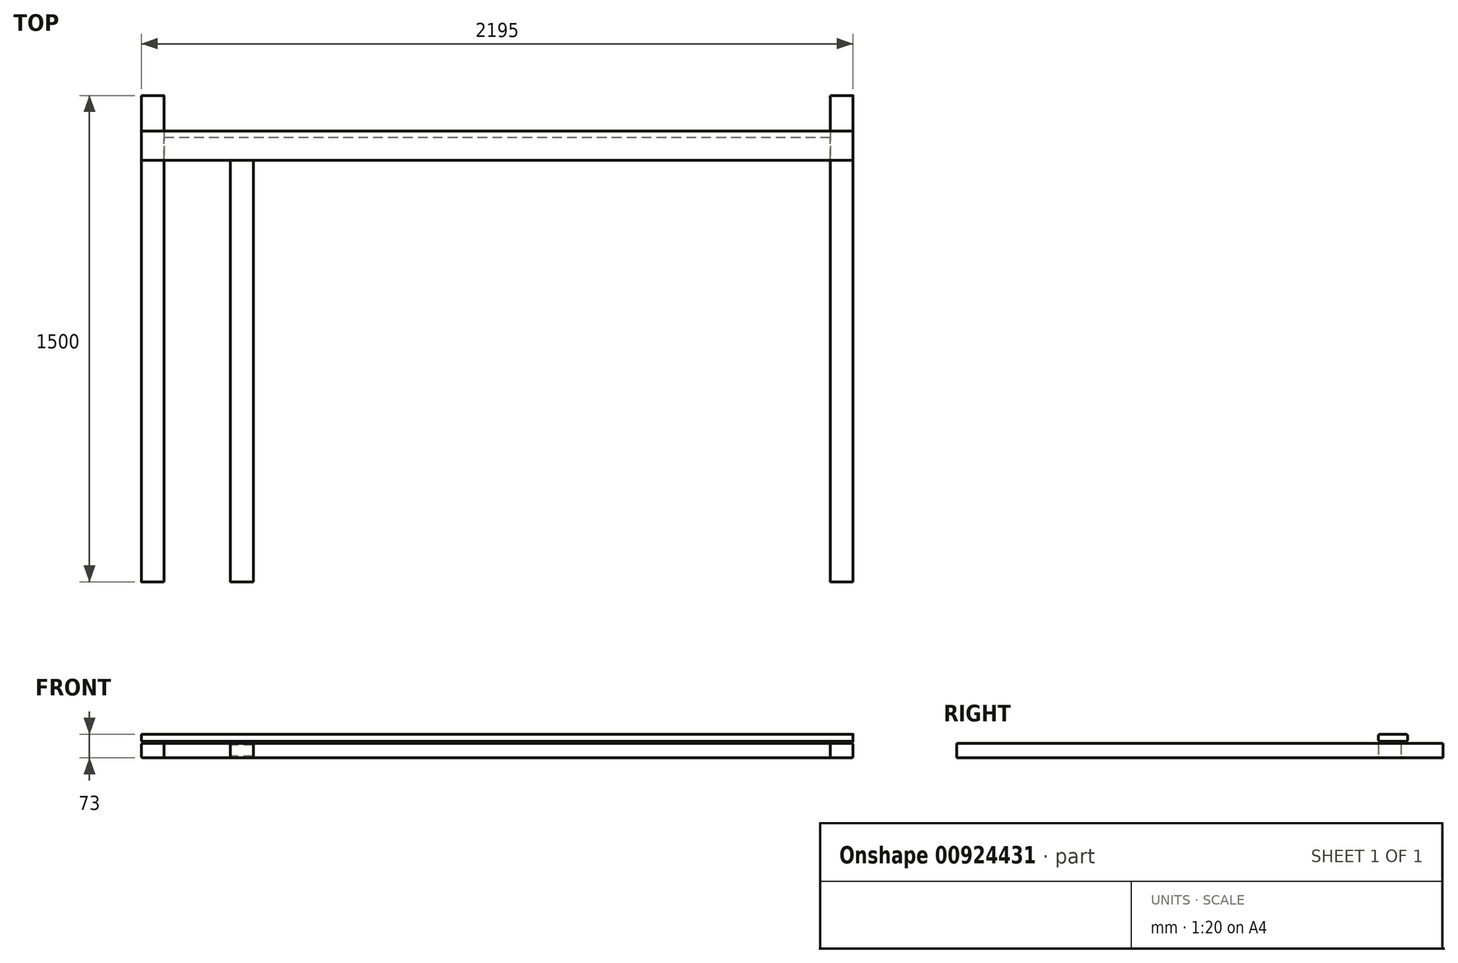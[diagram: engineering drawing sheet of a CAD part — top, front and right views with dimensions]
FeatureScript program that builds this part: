
annotation { "Feature Type Name" : "Feature", "Feature Type Description" : "" }
export const myFeature = defineFeature(function(context is Context, id is Id, definition is map)
    precondition{}
    {
        {
            var Q0;
            Q0=qCreatedBy(makeId("Front.planeOp"),FACE);
            var sketch = newSketch(context, id + "F0", { "sketchPlane" : qUnion([Q0])});
            skLineSegment(sketch, "E0.bottom", {"start": v(-5, 0) * mm, "end": v(-65, 0) * mm});
            skLineSegment(sketch, "E0.top", {"start": v(-5, 45) * mm, "end": v(-65, 45) * mm});
            skLineSegment(sketch, "E0.left", {"start": v(0, 5) * mm, "end": v(0, 40) * mm});
            skLineSegment(sketch, "E0.right", {"start": v(-70, 5) * mm, "end": v(-70, 40) * mm});
            skPoint(sketch, "E1.visualSharp", {"position": v(-70, 45) * mm});
            skArc(sketch, "E1.filletArc", {"start": v(-65, 45) * mm, "mid": v(-68.54, 43.54) * mm, "end": v(-70, 40) * mm});
            skPoint(sketch, "E2.visualSharp", {"position": v(0, 45) * mm});
            skArc(sketch, "E2.filletArc", {"start": v(0, 40) * mm, "mid": v(-1.46, 43.54) * mm, "end": v(-5, 45) * mm});
            skPoint(sketch, "E3.visualSharp", {"position": v(0, 0) * mm});
            skArc(sketch, "E3.filletArc", {"start": v(-5, 0) * mm, "mid": v(-1.46, 1.46) * mm, "end": v(0, 5) * mm});
            skPoint(sketch, "E4.visualSharp", {"position": v(-70, 0) * mm});
            skArc(sketch, "E4.filletArc", {"start": v(-70, 5) * mm, "mid": v(-68.54, 1.46) * mm, "end": v(-65, 0) * mm});
            skLineSegment(sketch, "E5.bottom", {"start": v(2060, 0) * mm, "end": v(2120, 0) * mm});
            skLineSegment(sketch, "E5.top", {"start": v(2060, 45) * mm, "end": v(2120, 45) * mm});
            skLineSegment(sketch, "E5.left", {"start": v(2055, 5) * mm, "end": v(2055, 40) * mm});
            skLineSegment(sketch, "E5.right", {"start": v(2125, 5) * mm, "end": v(2125, 40) * mm});
            skPoint(sketch, "E6.visualSharp", {"position": v(2055, 45) * mm});
            skArc(sketch, "E6.filletArc", {"start": v(2060, 45) * mm, "mid": v(2056.46, 43.54) * mm, "end": v(2055, 40) * mm});
            skPoint(sketch, "E7.visualSharp", {"position": v(2125, 45) * mm});
            skArc(sketch, "E7.filletArc", {"start": v(2125, 40) * mm, "mid": v(2123.54, 43.54) * mm, "end": v(2120, 45) * mm});
            skPoint(sketch, "E8.visualSharp", {"position": v(2125, 0) * mm});
            skArc(sketch, "E8.filletArc", {"start": v(2120, 0) * mm, "mid": v(2123.54, 1.46) * mm, "end": v(2125, 5) * mm});
            skPoint(sketch, "E9.visualSharp", {"position": v(2055, 0) * mm});
            skArc(sketch, "E9.filletArc", {"start": v(2055, 5) * mm, "mid": v(2056.46, 1.46) * mm, "end": v(2060, 0) * mm});
            skSolve(sketch);
        }
        {
            var Q0;
            Q0 = qSketchRegion(id + "F0", true);
            extrude(context, id + "F1", {"entities" : qUnion([Q0]), "oppositeDirection" : true, "depth" : 1500 * mm, "offsetDistance" : 25 * mm});
        }
        {
            var Q0;
            Q0=makeQuery(id+"F1.opExtrude","SWEPT_FACE",FACE,{"disambiguationData":[OSD([sQuery(id+"F0.wireOp",EDGE,"E0.left")])]});
            var sketch = newSketch(context, id + "F2", { "sketchPlane" : qUnion([Q0])});
            skLineSegment(sketch, "E10.bottom", {"start": v(1305, 45) * mm, "end": v(1365, 45) * mm});
            skLineSegment(sketch, "E10.top", {"start": v(1305, 0) * mm, "end": v(1365, 0) * mm});
            skLineSegment(sketch, "E10.left", {"start": v(1300, 40) * mm, "end": v(1300, 5) * mm});
            skLineSegment(sketch, "E10.right", {"start": v(1370, 40) * mm, "end": v(1370, 5) * mm});
            skPoint(sketch, "E11.visualSharp", {"position": v(1300, 45) * mm});
            skArc(sketch, "E11.filletArc", {"start": v(1305, 45) * mm, "mid": v(1301.46, 43.54) * mm, "end": v(1300, 40) * mm});
            skPoint(sketch, "E12.visualSharp", {"position": v(1370, 45) * mm});
            skArc(sketch, "E12.filletArc", {"start": v(1370, 40) * mm, "mid": v(1368.54, 43.54) * mm, "end": v(1365, 45) * mm});
            skPoint(sketch, "E13.visualSharp", {"position": v(1370, 0) * mm});
            skArc(sketch, "E13.filletArc", {"start": v(1365, 0) * mm, "mid": v(1368.54, 1.46) * mm, "end": v(1370, 5) * mm});
            skPoint(sketch, "E14.visualSharp", {"position": v(1300, 0) * mm});
            skArc(sketch, "E14.filletArc", {"start": v(1300, 5) * mm, "mid": v(1301.46, 1.46) * mm, "end": v(1305, 0) * mm});
            skSolve(sketch);
        }
        {
            var Q0;
            Q0 = qSketchRegion(id + "F2", true);
            extrude(context, id + "F3", {"entities" : qUnion([Q0]), "depth" : 2055 * mm, "offsetDistance" : 25 * mm});
        }
        {
            var Q0;
            Q0=makeQuery(id+"F3.opExtrude","SWEPT_FACE",FACE,{"disambiguationData":[OSD([sQuery(id+"F2.wireOp",EDGE,"E10.left")])]});
            var sketch = newSketch(context, id + "F4", { "sketchPlane" : qUnion([Q0])});
            skLineSegment(sketch, "E15.bottom", {"start": v(210, 45) * mm, "end": v(270, 45) * mm});
            skLineSegment(sketch, "E15.top", {"start": v(210, 0) * mm, "end": v(270, 0) * mm});
            skLineSegment(sketch, "E15.left", {"start": v(205, 40) * mm, "end": v(205, 5) * mm});
            skLineSegment(sketch, "E15.right", {"start": v(275, 40) * mm, "end": v(275, 5) * mm});
            skPoint(sketch, "E16.visualSharp", {"position": v(205, 45) * mm});
            skArc(sketch, "E16.filletArc", {"start": v(210, 45) * mm, "mid": v(206.46, 43.54) * mm, "end": v(205, 40) * mm});
            skPoint(sketch, "E17.visualSharp", {"position": v(275, 45) * mm});
            skArc(sketch, "E17.filletArc", {"start": v(275, 40) * mm, "mid": v(273.54, 43.54) * mm, "end": v(270, 45) * mm});
            skPoint(sketch, "E18.visualSharp", {"position": v(275, 0) * mm});
            skArc(sketch, "E18.filletArc", {"start": v(270, 0) * mm, "mid": v(273.54, 1.46) * mm, "end": v(275, 5) * mm});
            skPoint(sketch, "E19.visualSharp", {"position": v(205, 0) * mm});
            skArc(sketch, "E19.filletArc", {"start": v(205, 5) * mm, "mid": v(206.46, 1.46) * mm, "end": v(210, 0) * mm});
            skSolve(sketch);
        }
        {
            var Q0;
            Q0 = qSketchRegion(id + "F4", true);
            extrude(context, id + "F5", {"entities" : qUnion([Q0]), "operationType" : NewBodyOperationType.ADD, "depth" : 1300 * mm, "offsetDistance" : 25 * mm});
        }
        {
            var Q0;
            Q0=makeQuery(id+"F1.opExtrude","SWEPT_FACE",FACE,{"disambiguationData":[OSD([sQuery(id+"F0.wireOp",EDGE,"E0.right")])]});
            var sketch = newSketch(context, id + "F6", { "sketchPlane" : qUnion([Q0])});
            skLineSegment(sketch, "E20.bottom", {"start": v(-1305, 73) * mm, "end": v(-1385, 73) * mm});
            skLineSegment(sketch, "E20.top", {"start": v(-1305, 51) * mm, "end": v(-1385, 51) * mm});
            skLineSegment(sketch, "E20.left", {"start": v(-1300, 68) * mm, "end": v(-1300, 56) * mm});
            skLineSegment(sketch, "E20.right", {"start": v(-1390, 68) * mm, "end": v(-1390, 56) * mm});
            skPoint(sketch, "E21.visualSharp", {"position": v(-1390, 73) * mm});
            skArc(sketch, "E21.filletArc", {"start": v(-1385, 73) * mm, "mid": v(-1388.54, 71.54) * mm, "end": v(-1390, 68) * mm});
            skPoint(sketch, "E22.visualSharp", {"position": v(-1300, 73) * mm});
            skArc(sketch, "E22.filletArc", {"start": v(-1300, 68) * mm, "mid": v(-1301.46, 71.54) * mm, "end": v(-1305, 73) * mm});
            skPoint(sketch, "E23.visualSharp", {"position": v(-1390, 51) * mm});
            skArc(sketch, "E23.filletArc", {"start": v(-1390, 56) * mm, "mid": v(-1388.54, 52.46) * mm, "end": v(-1385, 51) * mm});
            skPoint(sketch, "E24.visualSharp", {"position": v(-1300, 51) * mm});
            skArc(sketch, "E24.filletArc", {"start": v(-1305, 51) * mm, "mid": v(-1301.46, 52.46) * mm, "end": v(-1300, 56) * mm});
            skSolve(sketch);
        }
        {
            var Q0;
            Q0=makeQuery(id+"F6.imprint","IMPRINT",FACE,{"disambiguationData":[TD([[makeQuery(id+"F6.imprint","IMPRINT",EDGE,{"derivedFrom":sQuery(id+"F6.wireOp",EDGE,"E20.bottom")}),1.0]])]});
            var Q1;
            Q1=makeQuery(id+"F1.opExtrude","SWEPT_FACE",FACE,{"disambiguationData":[OSD([sQuery(id+"F0.wireOp",EDGE,"E5.right")])]});
            extrude(context, id + "F7", {"entities" : qUnion([Q0]), "endBound" : BoundingType.UP_TO_SURFACE, "oppositeDirection" : true, "depth" : 25 * mm, "endBoundEntityFace" : qUnion([Q1]), "offsetDistance" : 25 * mm});
        }
    });
